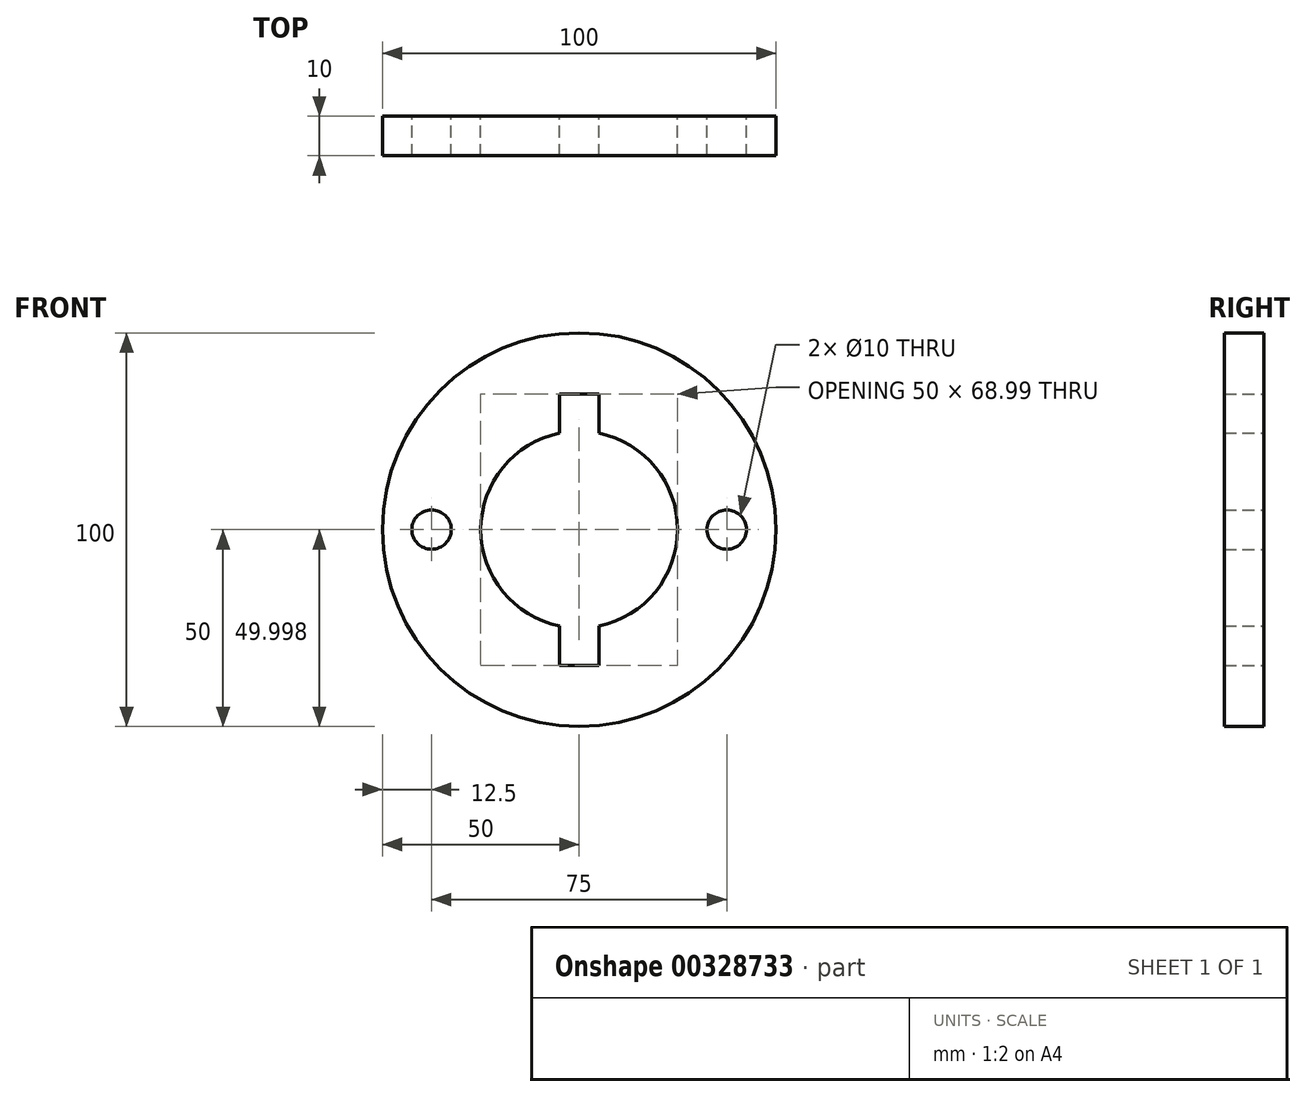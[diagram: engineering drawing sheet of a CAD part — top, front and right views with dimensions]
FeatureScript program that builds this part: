
annotation { "Feature Type Name" : "Feature", "Feature Type Description" : "" }
export const myFeature = defineFeature(function(context is Context, id is Id, definition is map)
    precondition{}
    {
        {
            var Q0;
            Q0=qCreatedBy(makeId("Front.planeOp"),FACE);
            var sketch = newSketch(context, id + "F0", { "sketchPlane" : qUnion([Q0])});
            skCircle(sketch, "E0", {"center": v(0, 0) * mm, "radius": 50 * mm});
            skArc(sketch, "E1", {"start": v(-5, 24.5) * mm, "mid": v(-25, 0.01) * mm, "end": v(-5.02, -24.5) * mm});
            skCircle(sketch, "E2", {"center": v(37.5, 0) * mm, "radius": 5 * mm});
            skCircle(sketch, "E3", {"center": v(-37.5, 0) * mm, "radius": 5 * mm});
            skLineSegment(sketch, "E4", {"start": v(0, 34.5) * mm, "end": v(-5, 34.5) * mm});
            skLineSegment(sketch, "E5", {"start": v(-5, 34.5) * mm, "end": v(-5, 24.5) * mm});
            skLineSegment(sketch, "E6", {"start": v(0, 34.5) * mm, "end": v(5, 34.5) * mm});
            skLineSegment(sketch, "E7", {"start": v(5, 34.5) * mm, "end": v(5, 24.5) * mm});
            skPoint(sketch, "E8.start.orphan", {"position": v(0, 25) * mm});
            skLineSegment(sketch, "E9", {"start": v(4.98, -24.5) * mm, "end": v(4.98, -34.5) * mm});
            skLineSegment(sketch, "E10", {"start": v(4.98, -34.5) * mm, "end": v(-5.02, -34.5) * mm});
            skLineSegment(sketch, "E11", {"start": v(-5.02, -34.5) * mm, "end": v(-5.02, -24.5) * mm});
            skArc(sketch, "E12.trimOffspring", {"start": v(4.98, -24.5) * mm, "mid": v(25, -0.01) * mm, "end": v(5, 24.5) * mm});
            skSolve(sketch);
        }
        {
            var Q0;
            Q0=makeQuery(id+"F0.imprint","IMPRINT",FACE,{"disambiguationData":[TD([[makeQuery(id+"F0.imprint","IMPRINT",EDGE,{"derivedFrom":sQuery(id+"F0.wireOp",EDGE,"E1")}),1.0]])]});
            var sketch = newSketch(context, id + "F1", { "sketchPlane" : qUnion([Q0])});
            skSolve(sketch);
        }
        {
            var Q0;
            Q0 = qSketchRegion(id + "F1", true);
            var Q1;
            Q1=makeQuery(id+"F0.imprint","IMPRINT",FACE,{"disambiguationData":[TD([[makeQuery(id+"F0.imprint","IMPRINT",EDGE,{"derivedFrom":sQuery(id+"F0.wireOp",EDGE,"E0")}),1.0]])]});
            extrude(context, id + "F2", {"entities" : qUnion([Q0, Q1]), "depth" : 10 * mm});
        }
    });
